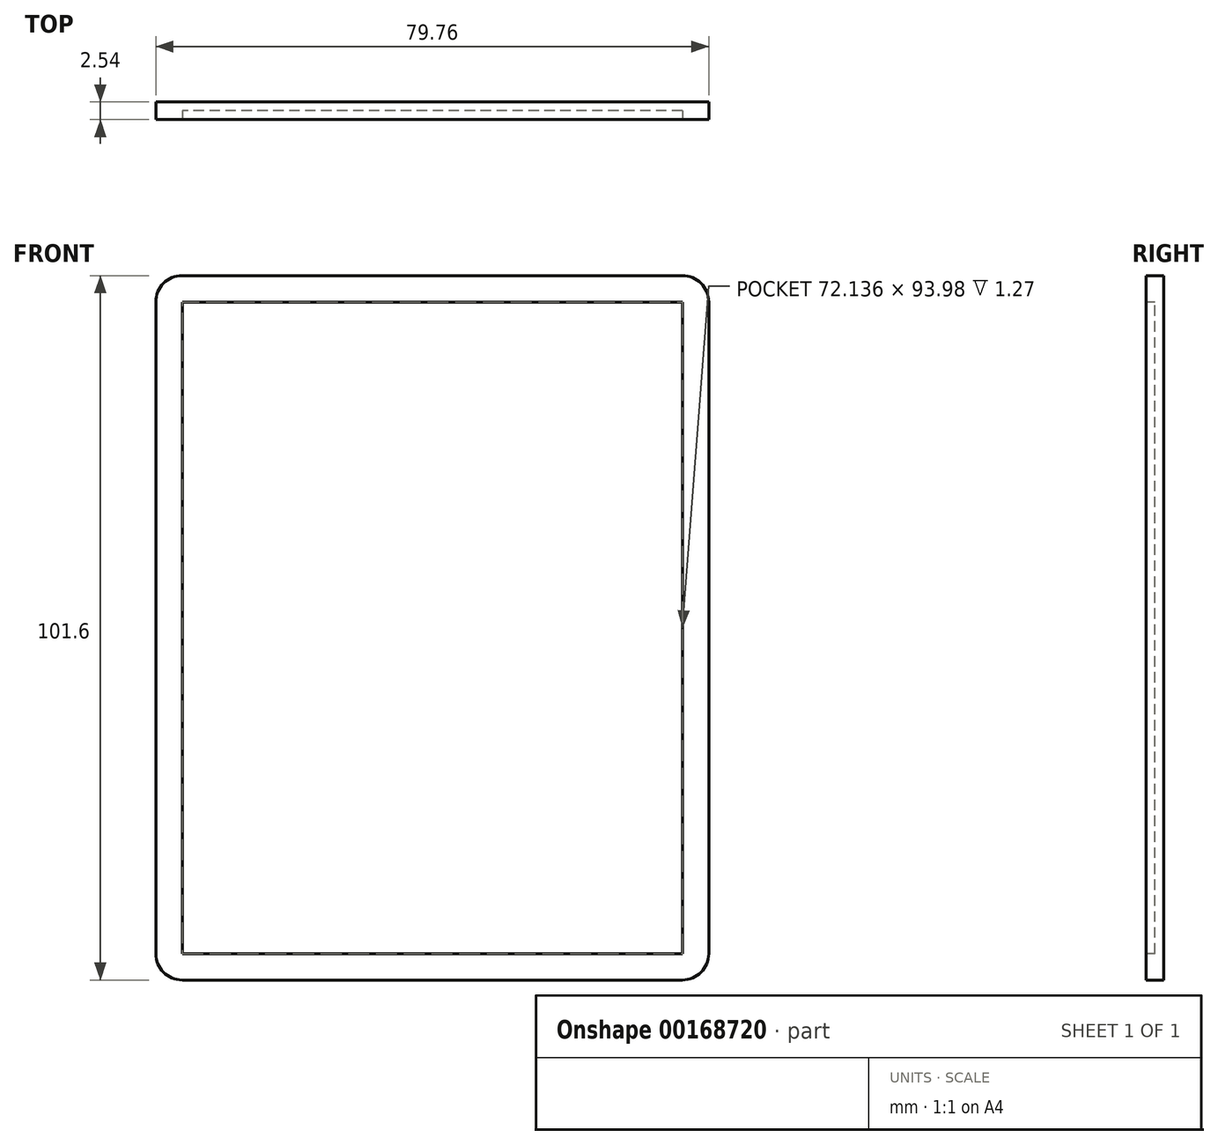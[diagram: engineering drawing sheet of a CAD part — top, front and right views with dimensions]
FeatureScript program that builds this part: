
annotation { "Feature Type Name" : "Feature", "Feature Type Description" : "" }
export const myFeature = defineFeature(function(context is Context, id is Id, definition is map)
    precondition{}
    {
        {
            var Q0;
            Q0=qCreatedBy(makeId("Front.planeOp"),FACE);
            var sketch = newSketch(context, id + "F0", { "sketchPlane" : qUnion([Q0])});
            skLineSegment(sketch, "E0.bottom", {"start": v(39.88, -50.8) * mm, "end": v(-39.88, -50.8) * mm});
            skLineSegment(sketch, "E0.top", {"start": v(39.88, 50.8) * mm, "end": v(-39.88, 50.8) * mm});
            skLineSegment(sketch, "E0.left", {"start": v(39.88, -50.8) * mm, "end": v(39.88, 50.8) * mm});
            skLineSegment(sketch, "E0.right", {"start": v(-39.88, -50.8) * mm, "end": v(-39.88, 50.8) * mm});
            skPoint(sketch, "E0.middle", {"position": v(0, 0) * mm});
            skSolve(sketch);
        }
        {
            var Q0;
            Q0 = qSketchRegion(id + "F0", true);
            extrude(context, id + "F1", {"entities" : qUnion([Q0]), "depth" : 2.54 * mm, "symmetric" : true});
        }
        {
            var Q0;
            Q0=makeQuery(id+"F1.opExtrude","SWEPT_EDGE",EDGE,{"disambiguationData":[OSD([sQuery(id+"F0.wireOp",EDGE,"E0.top"),sQuery(id+"F0.wireOp",EDGE,"E0.right")])]});
            var Q1;
            Q1=makeQuery(id+"F1.opExtrude","SWEPT_EDGE",EDGE,{"disambiguationData":[OSD([sQuery(id+"F0.wireOp",EDGE,"E0.top"),sQuery(id+"F0.wireOp",EDGE,"E0.left")])]});
            var Q2;
            Q2=makeQuery(id+"F1.opExtrude","SWEPT_EDGE",EDGE,{"disambiguationData":[OSD([sQuery(id+"F0.wireOp",EDGE,"E0.bottom"),sQuery(id+"F0.wireOp",EDGE,"E0.left")])]});
            var Q3;
            Q3=makeQuery(id+"F1.opExtrude","SWEPT_EDGE",EDGE,{"disambiguationData":[OSD([sQuery(id+"F0.wireOp",EDGE,"E0.bottom"),sQuery(id+"F0.wireOp",EDGE,"E0.right")])]});
            fillet(context, id + "F2", {"entities" : qUnion([Q0, Q1, Q2, Q3]), "radius" : 3.8 * mm, "tangentPropagation" : true, "allowEdgeOverflow" : false});
        }
        {
            var Q0;
            Q0=makeQuery(id+"F1.opExtrude","CAP_FACE",FACE,{"disambiguationData":[OSD([sQuery(id+"F0.wireOp",EDGE,"E0.bottom"),sQuery(id+"F0.wireOp",EDGE,"E0.top"),sQuery(id+"F0.wireOp",EDGE,"E0.left"),sQuery(id+"F0.wireOp",EDGE,"E0.right")])],"isStart":false});
            var sketch = newSketch(context, id + "F3", { "sketchPlane" : qUnion([Q0])});
            skLineSegment(sketch, "E1.bottom", {"start": v(36.07, -47) * mm, "end": v(-36.07, -47) * mm});
            skLineSegment(sketch, "E1.top", {"start": v(36.07, 47) * mm, "end": v(-36.07, 47) * mm});
            skLineSegment(sketch, "E1.left", {"start": v(36.07, -46.99) * mm, "end": v(36.07, 46.99) * mm});
            skLineSegment(sketch, "E1.right", {"start": v(-36.07, -46.99) * mm, "end": v(-36.07, 46.99) * mm});
            skPoint(sketch, "E1.middle", {"position": v(0, 0) * mm});
            skSolve(sketch);
        }
        {
            var Q0;
            Q0 = qSketchRegion(id + "F3", true);
            extrude(context, id + "F4", {"entities" : qUnion([Q0]), "operationType" : NewBodyOperationType.REMOVE, "oppositeDirection" : true, "depth" : 1.27 * mm});
        }
    });
